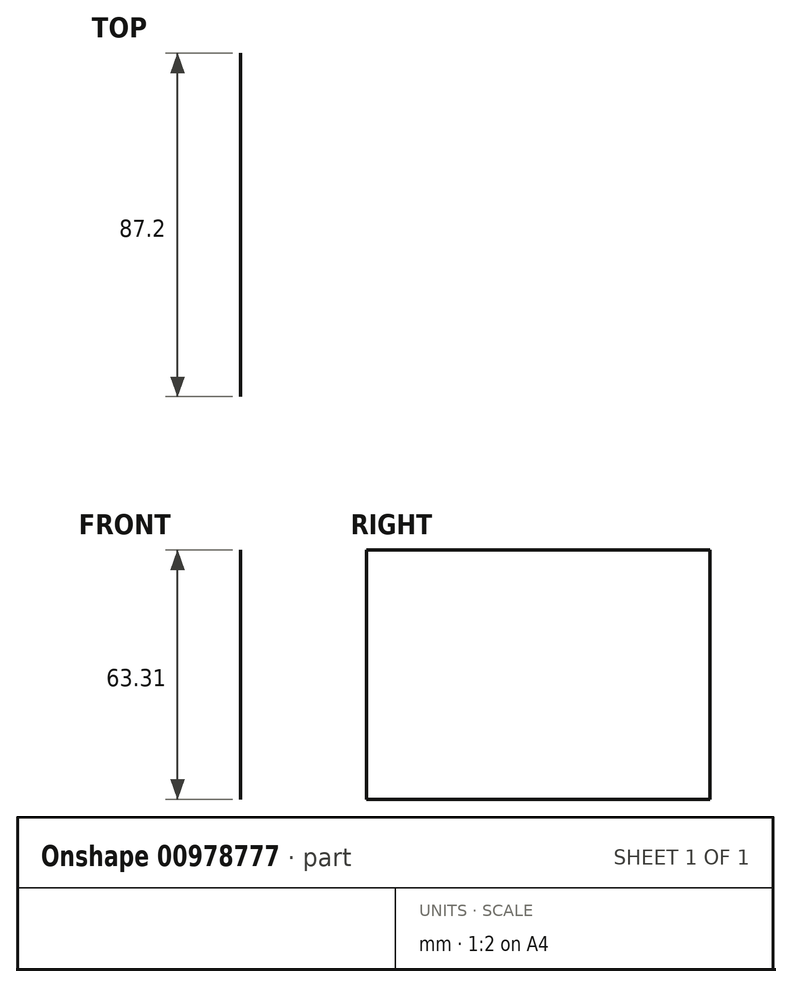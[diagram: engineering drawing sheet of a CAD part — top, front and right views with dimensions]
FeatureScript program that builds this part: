
annotation { "Feature Type Name" : "Feature", "Feature Type Description" : "" }
export const myFeature = defineFeature(function(context is Context, id is Id, definition is map)
    precondition{}
    {
        {
            var Q0;
            Q0=qCreatedBy(makeId("Front.planeOp"),FACE);
            var sketch = newSketch(context, id + "F0", { "sketchPlane" : qUnion([Q0])});
            skLineSegment(sketch, "E0", {"start": v(-134.56, 32.8) * mm, "end": v(-134.56, -30.5) * mm});
            skSolve(sketch);
        }
        {
            var Q0;
            Q0=sQuery(id+"F0.wireOp",EDGE,"E0");
            extrude(context, id + "F1", {"bodyType" : ToolBodyType.SURFACE, "surfaceEntities" : qUnion([Q0]), "depth" : 87.2 * mm, "offsetDistance" : 25 * mm});
        }
    });
